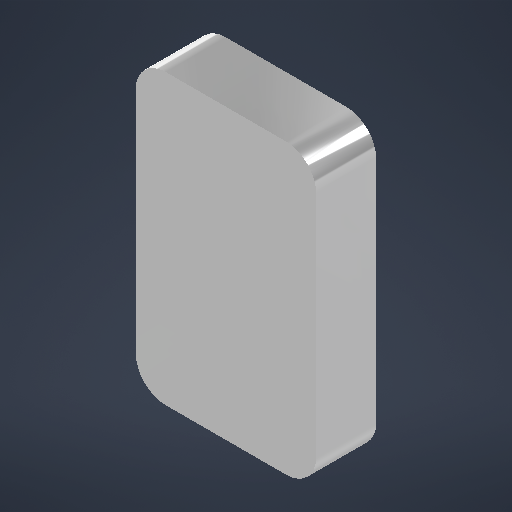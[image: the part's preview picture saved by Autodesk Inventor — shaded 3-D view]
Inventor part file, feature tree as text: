
AUTODESK INVENTOR PART (.ipt)
format: ipt  version: 2025.1 (Build 291241020, 241B)  size: 262,144 bytes
history: native  units: mm
features: reference x13, sketch x3, other x3, extrude x2, projected_geometry x2, hole x1
ambient origin geometry x8: Origin, YZ Plane, XZ Plane, XY Plane, X Axis, Y Axis, Z Axis, Center Point
bodies: Solid1 (feature_tree)
feature tree (24):
  extrude  "Extrusion1"  Depth=5.0mm
  hole  "Hole1"  [1 undecoded]
  extrude  "Extrusion2"  Depth=5.0mm
  sketch  "Sketch1"  dims[d0=10.0mm d1=0.0mm]
  reference  "Reference1"
  reference  "Reference2"
  reference  "Reference3"
  reference  "Reference4"
  reference  "Reference5"
  reference  "Reference6"
  reference  "Reference7"
  reference  "Reference8"
  sketch  "Sketch2"  dims[d3=2.459mm d4=6.0mm d5=4.0mm d6=2.0mm d7=90.0deg d8=8.0mm d9=20.594885mm d10=5.0mm]
  reference  "Reference9"
  reference  "Reference10"
  projected_geometry  "Projected Loop1"
  reference  "Reference11"
  reference  "Reference12"
  sketch  "Sketch3"  dims[d16=4.0mm d17=7.0mm d18=3.0mm d19=8.0mm d20=5.0mm d21=0.0mm]
  projected_geometry  "Projected Loop2"
  reference  "Reference13"
  other  "<userpath>\Documents\PicoProbe CAD\Main Assy.iam"
  other  "Main Assy.iam"
  other  "PicoProbe:1"
note: 1 required parameter value undecoded (feature->parameter linkage not recoverable at this tier; creation-order binding heuristic only, values carry confidence <= 0.55)
